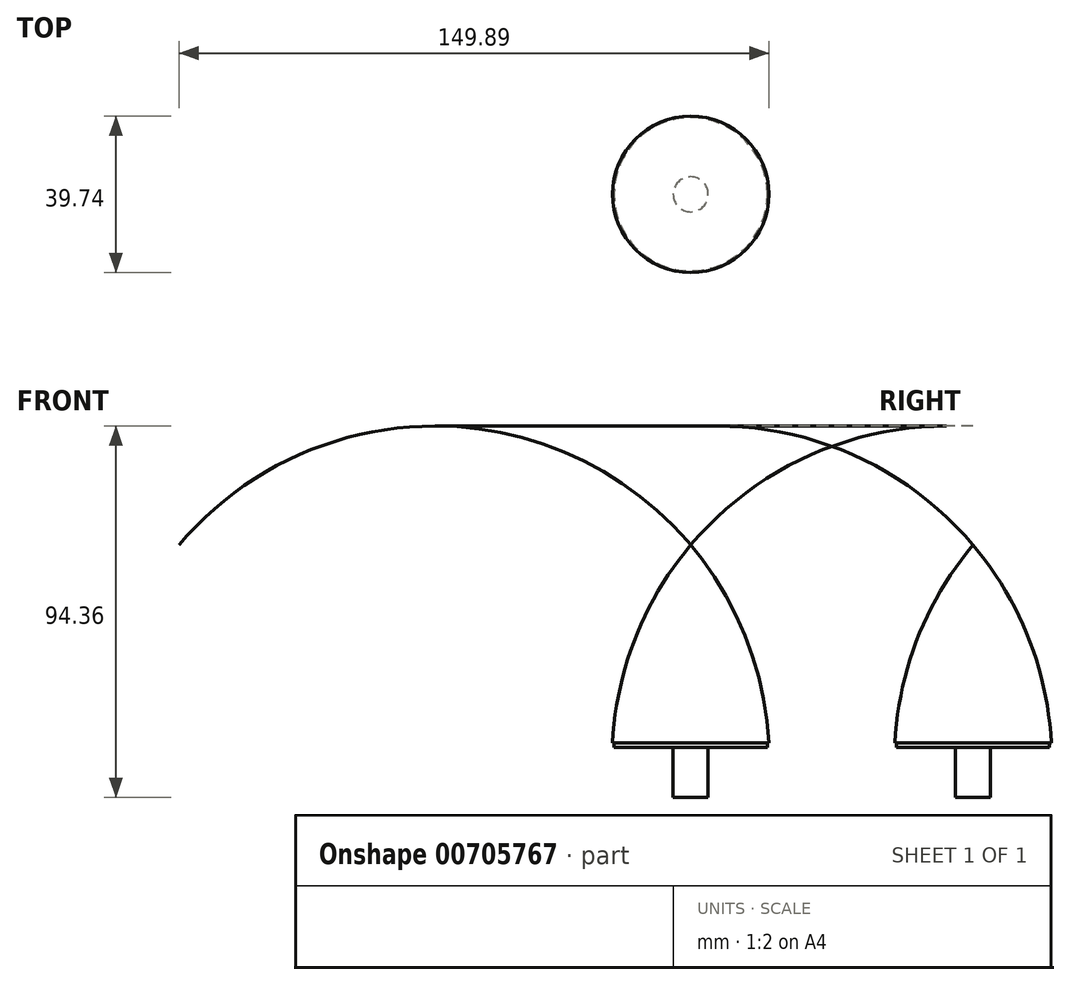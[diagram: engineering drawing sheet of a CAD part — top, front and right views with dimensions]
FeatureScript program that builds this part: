
annotation { "Feature Type Name" : "Feature", "Feature Type Description" : "" }
export const myFeature = defineFeature(function(context is Context, id is Id, definition is map)
    precondition{}
    {
        {
            var Q0;
            Q0=qCreatedBy(makeId("Front.planeOp"),FACE);
            var sketch = newSketch(context, id + "F0", { "sketchPlane" : qUnion([Q0])});
            skLineSegment(sketch, "E0", {"start": v(0, 81.7) * mm, "end": v(0, 84.7) * mm});
            skLineSegment(sketch, "E1", {"start": v(0, 0) * mm, "end": v(0, 50.8) * mm});
            skArc(sketch, "E2.0", {"start": v(19.87, 1.2) * mm, "mid": v(14.03, 27.92) * mm, "end": v(0, 51.42) * mm});
            skLineSegment(sketch, "E2.1", {"start": v(19.45, 1.2) * mm, "end": v(19.87, 1.2) * mm});
            skLineSegment(sketch, "E2.2", {"start": v(19.45, 0) * mm, "end": v(19.45, 1.2) * mm});
            skLineSegment(sketch, "E3", {"start": v(19.05, 0) * mm, "end": v(19.45, 0) * mm});
            skLineSegment(sketch, "E4", {"start": v(0, 50.8) * mm, "end": v(0, 51.42) * mm});
            skLineSegment(sketch, "E5", {"start": v(4.45, 0) * mm, "end": v(4.45, -12.7) * mm});
            skLineSegment(sketch, "E6", {"start": v(0, -12.7) * mm, "end": v(0, 0) * mm});
            skLineSegment(sketch, "E7", {"start": v(4.45, -12.7) * mm, "end": v(0, -12.7) * mm});
            skLineSegment(sketch, "E8", {"start": v(4.45, 0) * mm, "end": v(19.05, 0) * mm});
            skSolve(sketch);
        }
        {
            var Q0;
            Q0=makeQuery(id+"F0.imprint","IMPRINT",FACE,{"disambiguationData":[TD([[makeQuery(id+"F0.imprint","IMPRINT",EDGE,{"derivedFrom":sQuery(id+"F0.wireOp",EDGE,"E1")}),-1.0]])]});
            var Q1;
            Q1=sQuery(id+"F0.wireOp",EDGE,"E1");
            revolve(context, id + "F1", {"surfaceOperationType" : NewSurfaceOperationType.NEW, "entities" : qUnion([Q0]), "axis" : qUnion([Q1]), "revolveType" : RevolveType.FULL});
        }
    });
